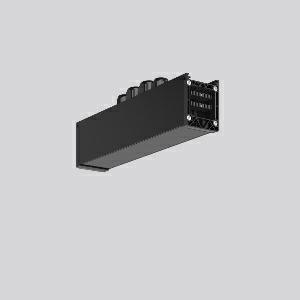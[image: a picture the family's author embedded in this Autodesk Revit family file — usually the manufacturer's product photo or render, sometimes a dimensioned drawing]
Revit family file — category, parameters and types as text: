
# Revit family: linedo_mitteleinspeisung_7pol_b_b_982698_003_4_8b21
name_source: partatom
category: Lighting Fixtures
units: mm (PartAtom-declared; Revit-internal decimal feet)

## family parameters
Cut with Voids When Loaded = No
Host = Face
Light Source = No
Part Type = Normal
Room Calculation Point = No
Round Connector Dimension = Use Diameter
Shared = No

## types (1)
- LINEDO_Mitteleinspeisung_7pol_B_B
    Apparent Load = 0 VA
    Default Elevation = 1800 mm
    Description = Series: LINEDO
Middle power feed, 7-pole, connection socket / socket. Housing: extruded aluminium profile, powder-coated. Cover made of plastic, surface like housing. LINEDO plug system, plastic, black. 4 cable glands (2 x M20 and 2 x M25). Cable glands on top. Easy connection for rigid or flexible wires.
Colour: black
Length: 312 mm
Width: 58 mm
Height: 76 mm
Weight: 751 g
    Height = 76 mm
    Lamp = 0 x
    Length = 312 mm
    Luminous efficacy = 0 lm/W
    Manufacturer = RZB
    ModVariant = No
    Model = 982698.003.4
    Mounting Place = Ceiling
    Mounting Type = Surface mounted, Pendant
    Number of Poles = 1
    OnlyDefault = Yes
    Power Factor = 1
    Product Name = LINEDO_Mitteleinspeisung_7pol_B_B
    Product group = Surface mounted continuous line luminaire system
    ProductGroupID = 310
    Protection Class = Protection class I
    Protection Degree = IP 54
    RLX_Detail_Level = 1
    RLX_Emergency_Light_Flux = 0 lm
    RLX_Emergency_Type = 0
    RLX_Emergency_Type_DB = No
    RlxData = <blob elided: 23549 chars, md5=fc0d886f>
    Standby Power = 0 W
    System Light Flux = 0 lm
    System Power = 0 W
    Type Comments = Product without accessories
    Type Image = 982698.003.1.jpg
    URL = http://relux.com
    VarID = ---
    Voltage = 0 V
    Weight = 0.00 kg
    Width = 58 mm

## geometry (parser evidence)
native form markers: Blend x4, Sweep x12
no freeform markers — native parametric forms only
